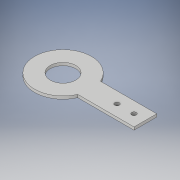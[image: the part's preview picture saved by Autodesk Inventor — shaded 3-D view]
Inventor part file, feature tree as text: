
AUTODESK INVENTOR PART (.ipt)
format: ipt  version: 2018 (Build 220112000, 112)  size: 116,224 bytes
history: native  units: in
note: dims shown in document units (in); Inventor stores cm internally (conversion verified against a paired STEP export)
features: extrude x1, sketch x1
ambient origin geometry x8: Origin, YZ Plane, XZ Plane, XY Plane, X Axis, Y Axis, Z Axis, Center Point
bodies: Solid1 (feature_tree)
feature tree (2):
  extrude  "Extrusion1"  Depth=0.5in
  sketch  "Sketch1"  dims[d1=2.0in d2=1.125in d3=1.125in d4=2.5in d6=0.75in d7=0.2031in d8=0.2031in d9=0.125in d10=0.0in d11=0.5in d14=0.5in]
